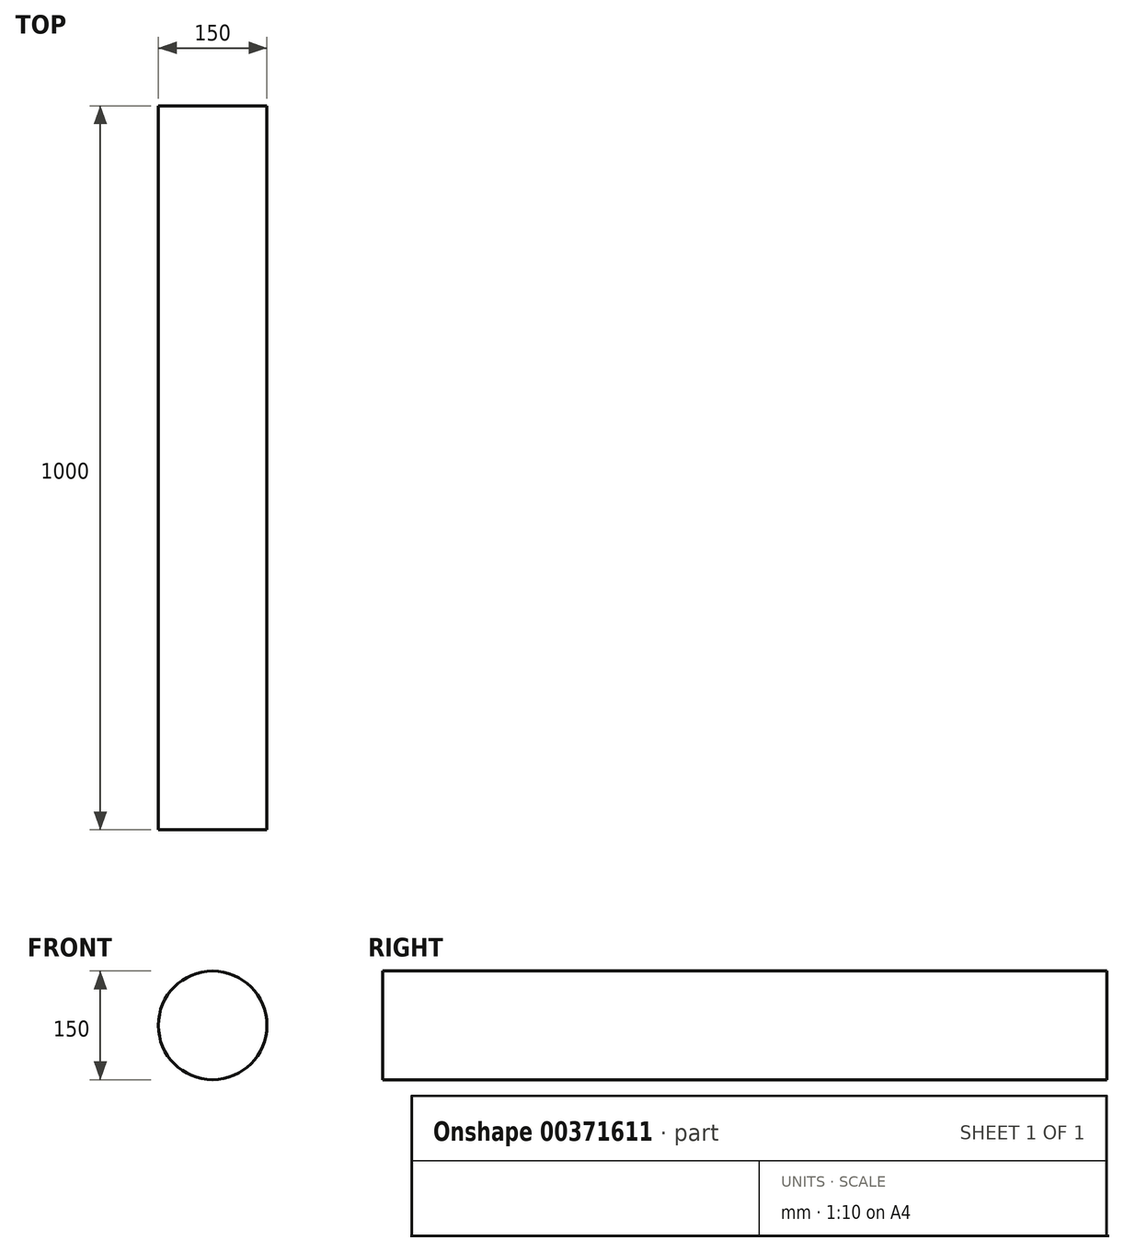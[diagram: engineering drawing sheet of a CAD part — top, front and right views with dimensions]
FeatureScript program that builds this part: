
annotation { "Feature Type Name" : "Feature", "Feature Type Description" : "" }
export const myFeature = defineFeature(function(context is Context, id is Id, definition is map)
    precondition{}
    {
        {
            var Q0;
            Q0=qCreatedBy(makeId("Front.planeOp"),FACE);
            var sketch = newSketch(context, id + "F0", { "sketchPlane" : qUnion([Q0])});
            skCircle(sketch, "E0", {"center": v(0, 0) * mm, "radius": 75 * mm});
            skSolve(sketch);
        }
        {
            var Q0;
            Q0=qSketchRegion(id+"F0",true);
            extrude(context, id + "F1", {"entities" : qUnion([Q0]), "oppositeDirection" : true, "depth" : 1000 * mm});
        }
    });
